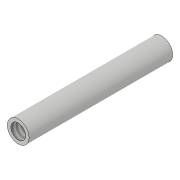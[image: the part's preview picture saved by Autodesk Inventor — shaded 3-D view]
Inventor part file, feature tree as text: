
AUTODESK INVENTOR PART (.ipt)
format: ipt  version: 2018.3 (Build 223284000, 284)  size: 78,848 bytes
history: native  units: in
note: dims shown in document units (in); Inventor stores cm internally (conversion verified against a paired STEP export)
features: extrude x1, hole x1, sketch x1
ambient origin geometry x8: Origin, YZ Plane, XZ Plane, XY Plane, X Axis, Y Axis, Z Axis, Center Point
bodies: Solid1 (feature_tree)
feature tree (3):
  extrude  "Extrusion1"  Depth=0.825in TaperAngle=0.0deg
  hole  "Hole1"  [1 undecoded]
  sketch  "Sketch1"  dims[d0=0.125in d2=0.825in d3=0.0in d15=1.0in d16=1.0in d6=0.085in d7=0.75in d8=0.375in d9=0.25in d10=0.5635in d11=0.349in d12=0.8108in]
note: 1 required parameter value undecoded (feature->parameter linkage not recoverable at this tier; creation-order binding heuristic only, values carry confidence <= 0.55)
